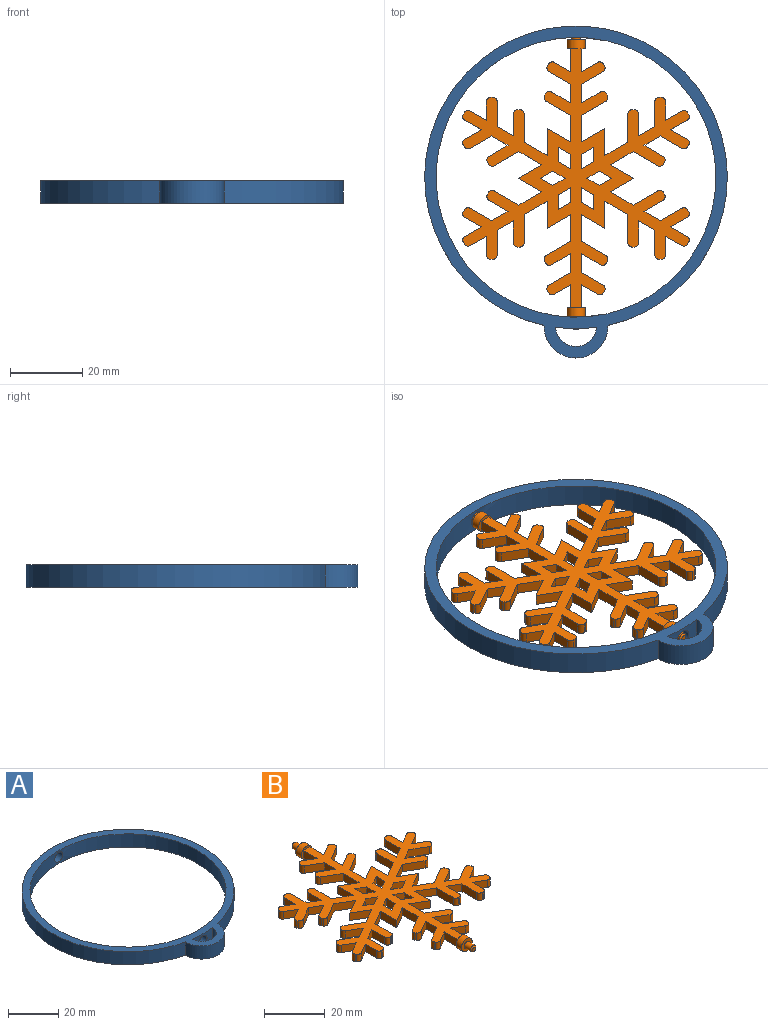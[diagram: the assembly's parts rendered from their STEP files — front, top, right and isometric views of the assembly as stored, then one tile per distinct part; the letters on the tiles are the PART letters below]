
ASSEMBLY  parts=2 mates=1
PART A: 9 faces, bbox 84.1x92.2x6.4 mm
  f0: cylinder r=42.04mm len=11.42mm, axis (0,0,-1), area 56.3mm2, adj f3,f4,f5,f7
  f1: cylinder r=42.04mm len=84.07mm, axis (0,0,-1), area 1546.9mm2, adj f3,f4,f6,f8
  f2: cylinder r=38.86mm len=77.72mm, axis (0,0,-1), area 1517.6mm2, adj f3,f4,f5,f6
  f3: plane 92.21x84.07mm, normal (0,0,1), area 879.1mm2, adj f0,f1,f2,f7,f8
  f4: plane 92.21x84.07mm, normal (0,0,-1), area 879.1mm2, adj f0,f1,f2,f7,f8
  f5: cylinder r=2.29mm len=4.57mm, axis (0,-1,0), area 45.6mm2, adj f0,f2
  f6: cylinder r=2.29mm len=4.57mm, axis (0,-1,0), area 45.6mm2, adj f1,f2
  f7: cylinder r=5.72mm len=11.42mm, axis (0,0,1), area 109.4mm2, adj f0,f3,f4
  f8: cylinder r=8.9mm len=17.79mm, axis (0,0,1), area 179.9mm2, adj f1,f3,f4
PART B: 218 faces, bbox 62.9x84x5 mm
  f0: plane 5x5mm, normal (0,1,0), area 14.7mm2, adj f2,f160
  f1: plane 5x5mm, normal (0,-1,0), area 10.6mm2, adj f2,f7,f9,f63,f64
  f2: cylinder r=2.5mm len=5mm, axis (0,1,0), area 39.3mm2, adj f0,f1
  f3: plane 5x5mm, normal (0,-1,0), area 14.7mm2, adj f4,f156
  f4: cylinder r=2.5mm len=5mm, axis (0,-1,0), area 39.3mm2, adj f3,f5
  f5: plane 5x5mm, normal (0,1,0), area 10.6mm2, adj f4,f6,f7,f8,f9
  f6: plane 6.4x3mm, normal (1,0,0), area 19.2mm2, adj f5,f7,f9,f10
  f7: plane 72x62.92mm, normal (0,0,-1), area 1369.7mm2, adj f1,f5,f6,f8,f10,f11,f12,f13
  f8: plane 6.4x3mm, normal (-1,0,0), area 19.2mm2, adj f5,f7,f9,f124
  f9: plane 72x62.92mm, normal (0,0,1), area 1369.7mm2, adj f1,f5,f6,f8,f10,f11,f12,f13
  f10: plane 4.44x3mm, normal (-0.5,-0.87,0), area 15.4mm2, adj f6,f7,f9,f200
  f11: plane 6.5x3.75mm, normal (-0.5,-0.87,0), area 22.5mm2, adj f7,f9,f12,f131
  f12: plane 7.5x3mm, normal (1,0,0), area 22.5mm2, adj f7,f9,f11,f13
  f13: plane 6.39x3.69mm, normal (-0.5,-0.87,0), area 22.1mm2, adj f7,f9,f12,f14
  f14: plane 7.8x3mm, normal (-1,0,0), area 23.4mm2, adj f7,f9,f13,f179
  f15: plane 3x0.46mm, normal (0,-1,0), area 1.4mm2, adj f7,f9,f179,f184
  f16: plane 6.06x3mm, normal (1,0,0), area 18.2mm2, adj f7,f9,f17,f184
  f17: plane 4.5x3mm, normal (-0.5,-0.87,0), area 15.6mm2, adj f7,f9,f16,f18
  f18: plane 6.86x3mm, normal (-1,0,0), area 20.6mm2, adj f7,f9,f17,f186
  f19: plane 3x0.46mm, normal (0,-1,0), area 1.4mm2, adj f7,f9,f186,f191
  f20: plane 5.13x3mm, normal (1,0,0), area 15.4mm2, adj f7,f9,f21,f191
  f21: plane 4.44x3mm, normal (-0.5,-0.87,0), area 15.4mm2, adj f7,f9,f20,f201
  f22: plane 3x0.4mm, normal (0.87,-0.5,0), area 1.4mm2, adj f7,f9,f201,f207
  f23: plane 4.44x3mm, normal (0.5,0.87,0), area 15.4mm2, adj f7,f9,f24,f207
  f24: plane 4.44x3mm, normal (0.5,-0.87,0), area 15.4mm2, adj f7,f9,f23,f163
  f25: plane 3x0.4mm, normal (0.87,0.5,0), area 1.4mm2, adj f7,f9,f163,f181
  f26: plane 5.94x3.43mm, normal (-0.5,0.87,0), area 20.6mm2, adj f7,f9,f27,f181
  f27: plane 4.5x3mm, normal (0.5,0.87,0), area 15.6mm2, adj f7,f9,f26,f28
  f28: plane 5.25x3.03mm, normal (0.5,-0.87,0), area 18.2mm2, adj f7,f9,f27,f199
  f29: plane 3x0.4mm, normal (0.87,0.5,0), area 1.4mm2, adj f7,f9,f199,f214
  f30: plane 6.75x3.9mm, normal (-0.5,0.87,0), area 23.4mm2, adj f7,f9,f31,f214
  f31: plane 6.39x3.69mm, normal (0.5,0.87,0), area 22.1mm2, adj f7,f9,f30,f32
  f32: plane 6.5x3.75mm, normal (0.5,-0.87,0), area 22.5mm2, adj f7,f9,f31,f33
  f33: plane 6.5x3.75mm, normal (0.5,0.87,0), area 22.5mm2, adj f7,f9,f32,f34
  f34: plane 6.39x3.69mm, normal (0.5,-0.87,0), area 22.1mm2, adj f7,f9,f33,f35
  f35: plane 6.75x3.9mm, normal (-0.5,-0.87,0), area 23.4mm2, adj f7,f9,f34,f176
  f36: plane 3x0.4mm, normal (0.87,-0.5,0), area 1.4mm2, adj f7,f9,f176,f193
  f37: plane 5.25x3.03mm, normal (0.5,0.87,0), area 18.2mm2, adj f7,f9,f38,f193
  f38: plane 4.5x3mm, normal (0.5,-0.87,0), area 15.6mm2, adj f7,f9,f37,f39
  f39: plane 5.94x3.43mm, normal (-0.5,-0.87,0), area 20.6mm2, adj f7,f9,f38,f190
  f40: plane 3x0.4mm, normal (0.87,-0.5,0), area 1.4mm2, adj f7,f9,f175,f190
  f41: plane 4.44x3mm, normal (0.5,0.87,0), area 15.4mm2, adj f7,f9,f42,f175
  f42: plane 4.44x3mm, normal (0.5,-0.87,0), area 15.4mm2, adj f7,f9,f41,f210
  f43: plane 3x0.4mm, normal (0.87,0.5,0), area 1.4mm2, adj f7,f9,f192,f210
  f44: plane 4.44x3mm, normal (-0.5,0.87,0), area 15.4mm2, adj f7,f9,f45,f192
  f45: plane 5.13x3mm, normal (1,0,0), area 15.4mm2, adj f7,f9,f44,f212
  f46: plane 3x0.46mm, normal (0,1,0), area 1.4mm2, adj f7,f9,f166,f212
  f47: plane 6.86x3mm, normal (-1,0,0), area 20.6mm2, adj f7,f9,f48,f166
  f48: plane 4.5x3mm, normal (-0.5,0.87,0), area 15.6mm2, adj f7,f9,f47,f49
  f49: plane 6.06x3mm, normal (1,0,0), area 18.2mm2, adj f7,f9,f48,f169
  f50: plane 3x0.46mm, normal (0,1,0), area 1.4mm2, adj f7,f9,f169,f197
  f51: plane 7.8x3mm, normal (-1,0,0), area 23.4mm2, adj f7,f9,f52,f197
  f52: plane 6.39x3.69mm, normal (-0.5,0.87,0), area 22.1mm2, adj f7,f9,f51,f53
  f53: plane 7.5x3mm, normal (1,0,0), area 22.5mm2, adj f7,f9,f52,f54
  f54: plane 6.5x3.75mm, normal (-0.5,0.87,0), area 22.5mm2, adj f7,f9,f53,f55
  f55: plane 7.38x3mm, normal (1,0,0), area 22.1mm2, adj f7,f9,f54,f56
  f56: plane 6.75x3.9mm, normal (0.5,-0.87,0), area 23.4mm2, adj f7,f9,f55,f209
  f57: plane 3x0.4mm, normal (0.87,0.5,0), area 1.4mm2, adj f7,f9,f202,f209
  f58: plane 5.25x3.03mm, normal (-0.5,0.87,0), area 18.2mm2, adj f7,f9,f59,f202
  f59: plane 5.2x3mm, normal (1,0,0), area 15.6mm2, adj f7,f9,f58,f60
  f60: plane 5.94x3.43mm, normal (0.5,-0.87,0), area 20.6mm2, adj f7,f9,f59,f216
  f61: plane 3x0.4mm, normal (0.87,0.5,0), area 1.4mm2, adj f7,f9,f208,f216
  f62: plane 4.44x3mm, normal (-0.5,0.87,0), area 15.4mm2, adj f7,f9,f63,f208
  f63: plane 6.4x3mm, normal (1,0,0), area 19.2mm2, adj f1,f7,f9,f62
  f64: plane 6.4x3mm, normal (-1,0,0), area 19.2mm2, adj f1,f7,f9,f65
  f65: plane 4.44x3mm, normal (0.5,0.87,0), area 15.4mm2, adj f7,f9,f64,f167
  f66: plane 3x0.4mm, normal (-0.87,0.5,0), area 1.4mm2, adj f7,f9,f167,f213
  f67: plane 5.94x3.43mm, normal (-0.5,-0.87,0), area 20.6mm2, adj f7,f9,f68,f213
  f68: plane 5.2x3mm, normal (-1,0,0), area 15.6mm2, adj f7,f9,f67,f69
  f69: plane 5.25x3.03mm, normal (0.5,0.87,0), area 18.2mm2, adj f7,f9,f68,f196
  f70: plane 3x0.4mm, normal (-0.87,0.5,0), area 1.4mm2, adj f7,f9,f171,f196
  f71: plane 6.75x3.9mm, normal (-0.5,-0.87,0), area 23.4mm2, adj f7,f9,f72,f171
  f72: plane 7.38x3mm, normal (-1,0,0), area 22.1mm2, adj f7,f9,f71,f73
  f73: plane 6.5x3.75mm, normal (0.5,0.87,0), area 22.5mm2, adj f7,f9,f72,f74
  f74: plane 7.5x3mm, normal (-1,0,0), area 22.5mm2, adj f7,f9,f73,f75
  f75: plane 6.39x3.69mm, normal (0.5,0.87,0), area 22.1mm2, adj f7,f9,f74,f76
  f76: plane 7.8x3mm, normal (1,0,0), area 23.4mm2, adj f7,f9,f75,f217
  f77: plane 3x0.46mm, normal (0,1,0), area 1.4mm2, adj f7,f9,f165,f217
  f78: plane 6.06x3mm, normal (-1,0,0), area 18.2mm2, adj f7,f9,f79,f165
  f79: plane 4.5x3mm, normal (0.5,0.87,0), area 15.6mm2, adj f7,f9,f78,f80
  f80: plane 6.86x3mm, normal (1,0,0), area 20.6mm2, adj f7,f9,f79,f174
  f81: plane 3x0.46mm, normal (0,1,0), area 1.4mm2, adj f7,f9,f174,f215
  f82: plane 5.13x3mm, normal (-1,0,0), area 15.4mm2, adj f7,f9,f83,f215
  f83: plane 4.44x3mm, normal (0.5,0.87,0), area 15.4mm2, adj f7,f9,f82,f189
  f84: plane 3x0.4mm, normal (-0.87,0.5,0), area 1.4mm2, adj f7,f9,f189,f205
  f85: plane 4.44x3mm, normal (-0.5,-0.87,0), area 15.4mm2, adj f7,f9,f86,f205
  f86: plane 4.44x3mm, normal (-0.5,0.87,0), area 15.4mm2, adj f7,f9,f85,f177
  f87: plane 3x0.4mm, normal (-0.87,-0.5,0), area 1.4mm2, adj f7,f9,f164,f177
  f88: plane 5.94x3.43mm, normal (0.5,-0.87,0), area 20.6mm2, adj f7,f9,f89,f164
  f89: plane 4.5x3mm, normal (-0.5,-0.87,0), area 15.6mm2, adj f7,f9,f88,f90
  f90: plane 5.25x3.03mm, normal (-0.5,0.87,0), area 18.2mm2, adj f7,f9,f89,f198
  f91: plane 3x0.4mm, normal (-0.87,-0.5,0), area 1.4mm2, adj f7,f9,f162,f198
  f92: plane 6.75x3.9mm, normal (0.5,-0.87,0), area 23.4mm2, adj f7,f9,f93,f162
  f93: plane 6.39x3.69mm, normal (-0.5,-0.87,0), area 22.1mm2, adj f7,f9,f92,f94
  f94: plane 6.5x3.75mm, normal (-0.5,0.87,0), area 22.5mm2, adj f7,f9,f93,f95
  f95: plane 6.5x3.75mm, normal (-0.5,-0.87,0), area 22.5mm2, adj f7,f9,f94,f96
  f96: plane 6.39x3.69mm, normal (-0.5,0.87,0), area 22.1mm2, adj f7,f9,f95,f97
  f97: plane 6.75x3.9mm, normal (0.5,0.87,0), area 23.4mm2, adj f7,f9,f96,f204
  f98: plane 3x0.4mm, normal (-0.87,0.5,0), area 1.4mm2, adj f7,f9,f188,f204
  f99: plane 5.25x3.03mm, normal (-0.5,-0.87,0), area 18.2mm2, adj f7,f9,f100,f188
  f100: plane 4.5x3mm, normal (-0.5,0.87,0), area 15.6mm2, adj f7,f9,f99,f101
  f101: plane 5.94x3.43mm, normal (0.5,0.87,0), area 20.6mm2, adj f7,f9,f100,f180
  f102: plane 3x0.4mm, normal (-0.87,0.5,0), area 1.4mm2, adj f7,f9,f180,f211
  f103: plane 4.44x3mm, normal (-0.5,-0.87,0), area 15.4mm2, adj f7,f9,f104,f211
  f104: plane 4.44x3mm, normal (-0.5,0.87,0), area 15.4mm2, adj f7,f9,f103,f172
  f105: plane 3x0.4mm, normal (-0.87,-0.5,0), area 1.4mm2, adj f7,f9,f172,f182
  f106: plane 4.44x3mm, normal (0.5,-0.87,0), area 15.4mm2, adj f7,f9,f107,f182
  f107: plane 5.13x3mm, normal (-1,0,0), area 15.4mm2, adj f7,f9,f106,f185
  f108: plane 3x0.46mm, normal (0,-1,0), area 1.4mm2, adj f7,f9,f185,f195
  f109: plane 6.86x3mm, normal (1,0,0), area 20.6mm2, adj f7,f9,f110,f195
  f110: plane 4.5x3mm, normal (0.5,-0.87,0), area 15.6mm2, adj f7,f9,f109,f111
  f111: plane 6.06x3mm, normal (-1,0,0), area 18.2mm2, adj f7,f9,f110,f206
  f112: plane 3x0.46mm, normal (0,-1,0), area 1.4mm2, adj f7,f9,f173,f206
  f113: plane 7.8x3mm, normal (1,0,0), area 23.4mm2, adj f7,f9,f114,f173
  f114: plane 6.39x3.69mm, normal (0.5,-0.87,0), area 22.1mm2, adj f7,f9,f113,f115
  f115: plane 7.5x3mm, normal (-1,0,0), area 22.5mm2, adj f7,f9,f114,f116
  f116: plane 6.5x3.75mm, normal (0.5,-0.87,0), area 22.5mm2, adj f7,f9,f115,f117
  f117: plane 7.38x3mm, normal (-1,0,0), area 22.1mm2, adj f7,f9,f116,f118
  f118: plane 6.75x3.9mm, normal (-0.5,0.87,0), area 23.4mm2, adj f7,f9,f117,f183
  f119: plane 3x0.4mm, normal (-0.87,-0.5,0), area 1.4mm2, adj f7,f9,f183,f187
  f120: plane 5.25x3.03mm, normal (0.5,-0.87,0), area 18.2mm2, adj f7,f9,f121,f187
  f121: plane 5.2x3mm, normal (-1,0,0), area 15.6mm2, adj f7,f9,f120,f122
  f122: plane 5.94x3.43mm, normal (-0.5,0.87,0), area 20.6mm2, adj f7,f9,f121,f170
  f123: plane 3x0.4mm, normal (-0.87,-0.5,0), area 1.4mm2, adj f7,f9,f170,f203
  f124: plane 4.44x3mm, normal (0.5,-0.87,0), area 15.4mm2, adj f7,f8,f9,f203
  f125: plane 3x0.4mm, normal (0.87,-0.5,0), area 1.4mm2, adj f7,f9,f194,f200
  f126: plane 5.94x3.43mm, normal (0.5,0.87,0), area 20.6mm2, adj f7,f9,f127,f194
  f127: plane 5.2x3mm, normal (1,0,0), area 15.6mm2, adj f7,f9,f126,f128
  f128: plane 5.25x3.03mm, normal (-0.5,-0.87,0), area 18.2mm2, adj f7,f9,f127,f168
  f129: plane 3x0.4mm, normal (0.87,-0.5,0), area 1.4mm2, adj f7,f9,f168,f178
  f130: plane 6.75x3.9mm, normal (0.5,0.87,0), area 23.4mm2, adj f7,f9,f131,f178
  f131: plane 7.38x3mm, normal (1,0,0), area 22.1mm2, adj f7,f9,f11,f130
  f132: plane 4.04x3mm, normal (-1,0,0), area 12.1mm2, adj f7,f9,f133,f135
  f133: plane 3.5x3mm, normal (-0.5,0.87,0), area 12.1mm2, adj f7,f9,f132,f134
  f134: plane 4.04x3mm, normal (1,0,0), area 12.1mm2, adj f7,f9,f133,f135
  f135: plane 3.5x3mm, normal (0.5,-0.87,0), area 12.1mm2, adj f7,f9,f132,f134
  f136: plane 4.04x3mm, normal (1,0,0), area 12.1mm2, adj f7,f9,f137,f139
  f137: plane 3.5x3mm, normal (-0.5,-0.87,0), area 12.1mm2, adj f7,f9,f136,f138
  f138: plane 4.04x3mm, normal (-1,0,0), area 12.1mm2, adj f7,f9,f137,f139
  f139: plane 3.5x3mm, normal (0.5,0.87,0), area 12.1mm2, adj f7,f9,f136,f138
  f140: plane 3.5x3mm, normal (-0.5,0.87,0), area 12.1mm2, adj f7,f9,f141,f143
  f141: plane 4.04x3mm, normal (1,0,0), area 12.1mm2, adj f7,f9,f140,f142
  f142: plane 3.5x3mm, normal (0.5,-0.87,0), area 12.1mm2, adj f7,f9,f141,f143
  f143: plane 4.04x3mm, normal (-1,0,0), area 12.1mm2, adj f7,f9,f140,f142
  f144: plane 4.04x3mm, normal (-1,0,0), area 12.1mm2, adj f7,f9,f145,f147
  f145: plane 3.5x3mm, normal (0.5,0.87,0), area 12.1mm2, adj f7,f9,f144,f146
  f146: plane 4.04x3mm, normal (1,0,0), area 12.1mm2, adj f7,f9,f145,f147
  f147: plane 3.5x3mm, normal (-0.5,-0.87,0), area 12.1mm2, adj f7,f9,f144,f146
  f148: plane 3.5x3mm, normal (0.5,-0.87,0), area 12.1mm2, adj f7,f9,f149,f151
  f149: plane 3.5x3mm, normal (-0.5,-0.87,0), area 12.1mm2, adj f7,f9,f148,f150
  f150: plane 3.5x3mm, normal (-0.5,0.87,0), area 12.1mm2, adj f7,f9,f149,f151
  f151: plane 3.5x3mm, normal (0.5,0.87,0), area 12.1mm2, adj f7,f9,f148,f150
  f152: plane 3.5x3mm, normal (0.5,0.87,0), area 12.1mm2, adj f7,f9,f153,f155
  f153: plane 3.5x3mm, normal (0.5,-0.87,0), area 12.1mm2, adj f7,f9,f152,f154
  f154: plane 3.5x3mm, normal (-0.5,-0.87,0), area 12.1mm2, adj f7,f9,f153,f155
  f155: plane 3.5x3mm, normal (-0.5,0.87,0), area 12.1mm2, adj f7,f9,f152,f154
  f156: cylinder r=1.25mm len=3mm, axis (0,-1,0), area 23.6mm2, adj f3,f158
  f157: plane 1.5x1.5mm, normal (0,-1,0), area 1.8mm2, adj f158
  f158: cone r=1mm half-angle=45deg, axis (0,1,0), area 4.4mm2, adj f156,f157
  f159: plane 1.5x1.5mm, normal (0,1,0), area 1.8mm2, adj f161
  f160: cylinder r=1.25mm len=3mm, axis (0,-1,0), area 23.6mm2, adj f0,f161
  f161: cone r=1mm half-angle=45deg, axis (0,-1,0), area 4.4mm2, adj f159,f160
  f162: cylinder r=1.27mm len=3mm, axis (0,0,-1), area 6mm2, adj f7,f9,f91,f92
  f163: cylinder r=1.27mm len=3mm, axis (0,0,1), area 6mm2, adj f7,f9,f24,f25
  f164: cylinder r=1.27mm len=3mm, axis (0,0,-1), area 6mm2, adj f7,f9,f87,f88
  f165: cylinder r=1.27mm len=3mm, axis (0,0,-1), area 6mm2, adj f7,f9,f77,f78
  f166: cylinder r=1.27mm len=3mm, axis (0,0,-1), area 6mm2, adj f7,f9,f46,f47
  f167: cylinder r=1.27mm len=3mm, axis (0,0,1), area 6mm2, adj f7,f9,f65,f66
  f168: cylinder r=1.27mm len=3mm, axis (0,0,1), area 6mm2, adj f7,f9,f128,f129
  f169: cylinder r=1.27mm len=3mm, axis (0,0,1), area 6mm2, adj f7,f9,f49,f50
  f170: cylinder r=1.27mm len=3mm, axis (0,0,1), area 6mm2, adj f7,f9,f122,f123
  f171: cylinder r=1.27mm len=3mm, axis (0,0,-1), area 6mm2, adj f7,f9,f70,f71
  f172: cylinder r=1.27mm len=3mm, axis (0,0,1), area 6mm2, adj f7,f9,f104,f105
  f173: cylinder r=1.27mm len=3mm, axis (0,0,-1), area 6mm2, adj f7,f9,f112,f113
  f174: cylinder r=1.27mm len=3mm, axis (0,0,1), area 6mm2, adj f7,f9,f80,f81
  f175: cylinder r=1.27mm len=3mm, axis (0,0,-1), area 6mm2, adj f7,f9,f40,f41
  f176: cylinder r=1.27mm len=3mm, axis (0,0,1), area 6mm2, adj f7,f9,f35,f36
  f177: cylinder r=1.27mm len=3mm, axis (0,0,1), area 6mm2, adj f7,f9,f86,f87
  f178: cylinder r=1.27mm len=3mm, axis (0,0,-1), area 6mm2, adj f7,f9,f129,f130
  f179: cylinder r=1.27mm len=3mm, axis (0,0,1), area 6mm2, adj f7,f9,f14,f15
  f180: cylinder r=1.27mm len=3mm, axis (0,0,1), area 6mm2, adj f7,f9,f101,f102
  f181: cylinder r=1.27mm len=3mm, axis (0,0,-1), area 6mm2, adj f7,f9,f25,f26
  f182: cylinder r=1.27mm len=3mm, axis (0,0,-1), area 6mm2, adj f7,f9,f105,f106
  f183: cylinder r=1.27mm len=3mm, axis (0,0,1), area 6mm2, adj f7,f9,f118,f119
  f184: cylinder r=1.27mm len=3mm, axis (0,0,-1), area 6mm2, adj f7,f9,f15,f16
  f185: cylinder r=1.27mm len=3mm, axis (0,0,1), area 6mm2, adj f7,f9,f107,f108
  f186: cylinder r=1.27mm len=3mm, axis (0,0,1), area 6mm2, adj f7,f9,f18,f19
  f187: cylinder r=1.27mm len=3mm, axis (0,0,-1), area 6mm2, adj f7,f9,f119,f120
  f188: cylinder r=1.27mm len=3mm, axis (0,0,-1), area 6mm2, adj f7,f9,f98,f99
  f189: cylinder r=1.27mm len=3mm, axis (0,0,1), area 6mm2, adj f7,f9,f83,f84
  f190: cylinder r=1.27mm len=3mm, axis (0,0,1), area 6mm2, adj f7,f9,f39,f40
  f191: cylinder r=1.27mm len=3mm, axis (0,0,-1), area 6mm2, adj f7,f9,f19,f20
  f192: cylinder r=1.27mm len=3mm, axis (0,0,-1), area 6mm2, adj f7,f9,f43,f44
  f193: cylinder r=1.27mm len=3mm, axis (0,0,-1), area 6mm2, adj f7,f9,f36,f37
  f194: cylinder r=1.27mm len=3mm, axis (0,0,-1), area 6mm2, adj f7,f9,f125,f126
  f195: cylinder r=1.27mm len=3mm, axis (0,0,-1), area 6mm2, adj f7,f9,f108,f109
  f196: cylinder r=1.27mm len=3mm, axis (0,0,1), area 6mm2, adj f7,f9,f69,f70
  f197: cylinder r=1.27mm len=3mm, axis (0,0,-1), area 6mm2, adj f7,f9,f50,f51
  f198: cylinder r=1.27mm len=3mm, axis (0,0,1), area 6mm2, adj f7,f9,f90,f91
  f199: cylinder r=1.27mm len=3mm, axis (0,0,1), area 6mm2, adj f7,f9,f28,f29
  f200: cylinder r=1.27mm len=3mm, axis (0,0,1), area 6mm2, adj f7,f9,f10,f125
  f201: cylinder r=1.27mm len=3mm, axis (0,0,1), area 6mm2, adj f7,f9,f21,f22
  f202: cylinder r=1.27mm len=3mm, axis (0,0,-1), area 6mm2, adj f7,f9,f57,f58
  f203: cylinder r=1.27mm len=3mm, axis (0,0,-1), area 6mm2, adj f7,f9,f123,f124
  f204: cylinder r=1.27mm len=3mm, axis (0,0,1), area 6mm2, adj f7,f9,f97,f98
  f205: cylinder r=1.27mm len=3mm, axis (0,0,-1), area 6mm2, adj f7,f9,f84,f85
  f206: cylinder r=1.27mm len=3mm, axis (0,0,1), area 6mm2, adj f7,f9,f111,f112
  f207: cylinder r=1.27mm len=3mm, axis (0,0,-1), area 6mm2, adj f7,f9,f22,f23
  f208: cylinder r=1.27mm len=3mm, axis (0,0,-1), area 6mm2, adj f7,f9,f61,f62
  f209: cylinder r=1.27mm len=3mm, axis (0,0,1), area 6mm2, adj f7,f9,f56,f57
  f210: cylinder r=1.27mm len=3mm, axis (0,0,1), area 6mm2, adj f7,f9,f42,f43
  f211: cylinder r=1.27mm len=3mm, axis (0,0,-1), area 6mm2, adj f7,f9,f102,f103
  f212: cylinder r=1.27mm len=3mm, axis (0,0,1), area 6mm2, adj f7,f9,f45,f46
  f213: cylinder r=1.27mm len=3mm, axis (0,0,-1), area 6mm2, adj f7,f9,f66,f67
  f214: cylinder r=1.27mm len=3mm, axis (0,0,-1), area 6mm2, adj f7,f9,f29,f30
  f215: cylinder r=1.27mm len=3mm, axis (0,0,-1), area 6mm2, adj f7,f9,f81,f82
  f216: cylinder r=1.27mm len=3mm, axis (0,0,1), area 6mm2, adj f7,f9,f60,f61
  f217: cylinder r=1.27mm len=3mm, axis (0,0,1), area 6mm2, adj f7,f9,f76,f77
PLACE A at identity fixed
PLACE B t=(0,-0.27,3.18)mm
MATE cylindrical B.f4 <-> A.f5  axis (0,-1,0) through (0,-38.77,3.18)mm
